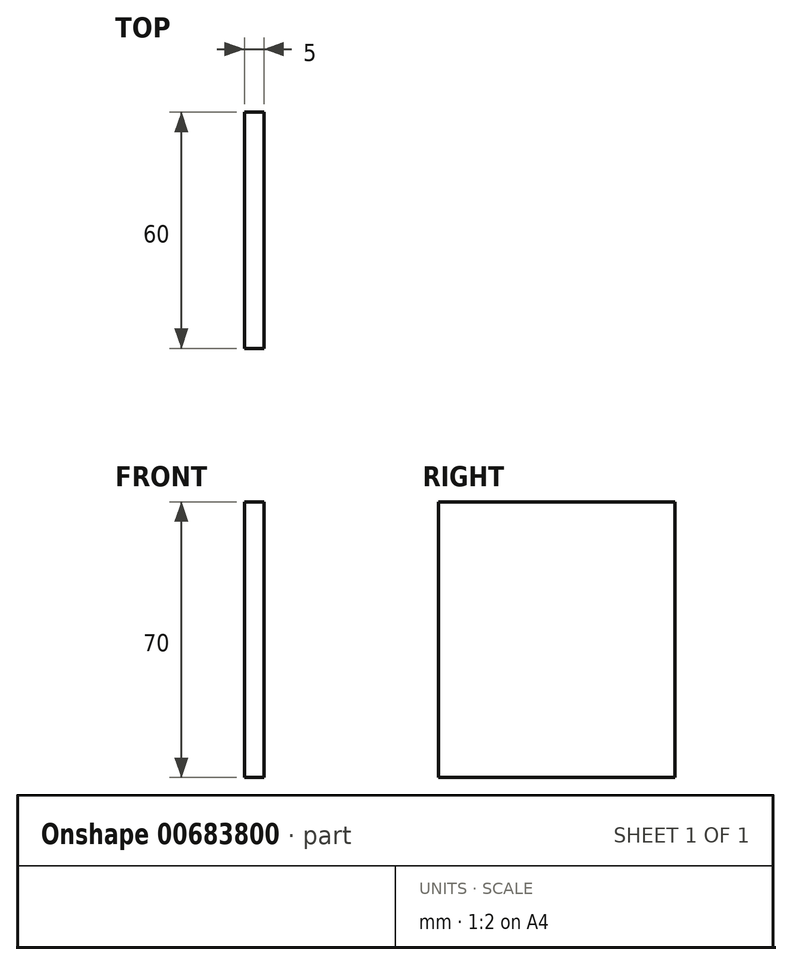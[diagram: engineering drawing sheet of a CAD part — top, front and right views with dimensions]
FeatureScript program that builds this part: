
annotation { "Feature Type Name" : "Feature", "Feature Type Description" : "" }
export const myFeature = defineFeature(function(context is Context, id is Id, definition is map)
    precondition{}
    {
        {
            var Q0;
            Q0=qCreatedBy(makeId("Right.planeOp"),FACE);
            var sketch = newSketch(context, id + "F0", { "sketchPlane" : qUnion([Q0])});
            skLineSegment(sketch, "E0.bottom", {"start": v(0, 0) * mm, "end": v(60, 0) * mm});
            skLineSegment(sketch, "E0.top", {"start": v(0, -70) * mm, "end": v(60, -70) * mm});
            skLineSegment(sketch, "E0.left", {"start": v(0, 0) * mm, "end": v(0, -70) * mm});
            skLineSegment(sketch, "E0.right", {"start": v(60, 0) * mm, "end": v(60, -70) * mm});
            skSolve(sketch);
        }
        {
            var Q0;
            Q0=makeQuery(id+"F0.imprint","IMPRINT",FACE,{"disambiguationData":[TD([[makeQuery(id+"F0.imprint","IMPRINT",EDGE,{"derivedFrom":sQuery(id+"F0.wireOp",EDGE,"E0.bottom")}),-1.0]])]});
            extrude(context, id + "F1", {"entities" : qUnion([Q0]), "depth" : 5 * mm, "offsetDistance" : 25 * mm});
        }
    });
